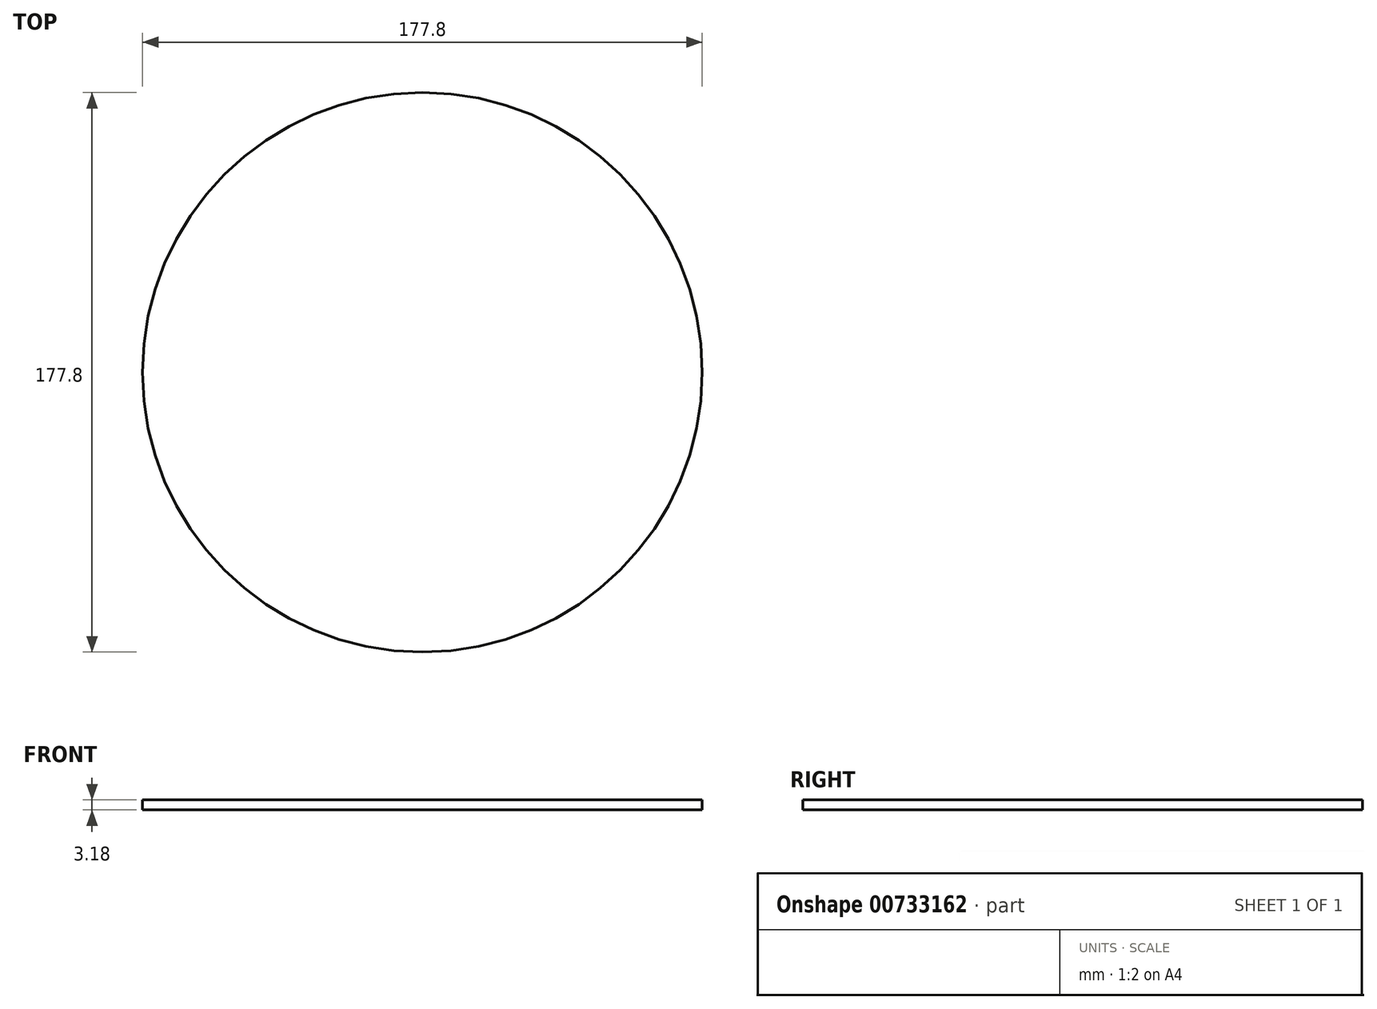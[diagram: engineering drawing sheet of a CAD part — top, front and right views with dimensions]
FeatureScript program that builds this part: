
annotation { "Feature Type Name" : "Feature", "Feature Type Description" : "" }
export const myFeature = defineFeature(function(context is Context, id is Id, definition is map)
    precondition{}
    {
        {
            var Q0;
            Q0=qCreatedBy(makeId("Top.planeOp"),FACE);
            var sketch = newSketch(context, id + "F0", { "sketchPlane" : qUnion([Q0])});
            skCircle(sketch, "E0", {"center": v(0, 0) * mm, "radius": 88.9 * mm});
            skSolve(sketch);
        }
        {
            var Q0;
            Q0 = qSketchRegion(id + "F0", true);
            extrude(context, id + "F1", {"entities" : qUnion([Q0]), "depth" : 3.17 * mm, "offsetDistance" : 25.4 * mm});
        }
    });
